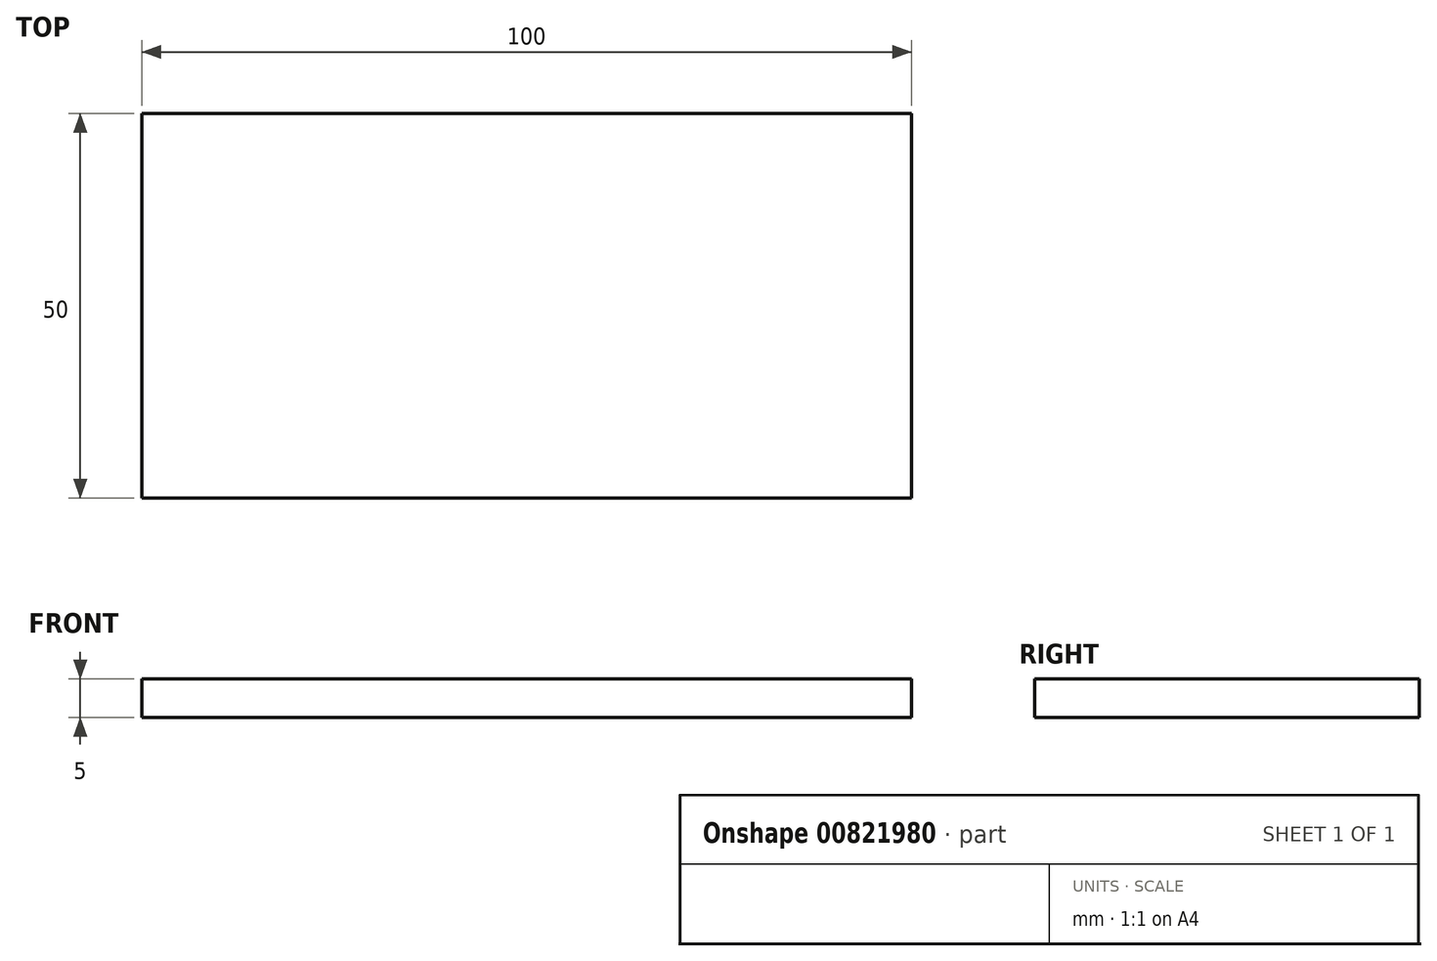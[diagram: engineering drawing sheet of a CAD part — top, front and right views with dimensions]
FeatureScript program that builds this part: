
annotation { "Feature Type Name" : "Feature", "Feature Type Description" : "" }
export const myFeature = defineFeature(function(context is Context, id is Id, definition is map)
    precondition{}
    {
        {
            var Q0;
            Q0=qCreatedBy(makeId("Top.planeOp"),FACE);
            var sketch = newSketch(context, id + "F0", { "sketchPlane" : qUnion([Q0])});
            skLineSegment(sketch, "E0.bottom", {"start": v(0, 0) * mm, "end": v(100, 0) * mm});
            skLineSegment(sketch, "E0.top", {"start": v(0, 50) * mm, "end": v(100, 50) * mm});
            skLineSegment(sketch, "E0.left", {"start": v(0, 0) * mm, "end": v(0, 50) * mm});
            skLineSegment(sketch, "E0.right", {"start": v(100, 0) * mm, "end": v(100, 50) * mm});
            skSolve(sketch);
        }
        {
            var Q0;
            Q0=makeQuery(id+"F0.imprint","IMPRINT",FACE,{"disambiguationData":[TD([[makeQuery(id+"F0.imprint","IMPRINT",EDGE,{"derivedFrom":sQuery(id+"F0.wireOp",EDGE,"E0.bottom")}),1.0]])]});
            extrude(context, id + "F1", {"entities" : qUnion([Q0]), "depth" : 5 * mm, "offsetDistance" : 25 * mm});
        }
    });
